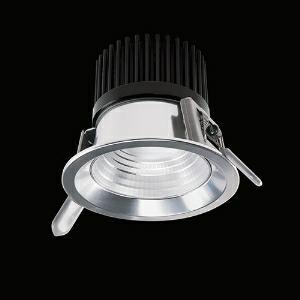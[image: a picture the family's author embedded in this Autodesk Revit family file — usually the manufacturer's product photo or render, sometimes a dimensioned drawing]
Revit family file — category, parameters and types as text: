
# Revit family: spectral_myral_myral_4500-840-f
name_source: partatom
category: Lighting Fixtures
revit_build: Autodesk Revit 2016 (Build: 20150220_1215(x64)
units: mm (PartAtom-declared; Revit-internal decimal feet)

## family parameters
Cut with Voids When Loaded = No
Host = Face
Light Source = No
Part Type = Normal
Room Calculation Point = No
Round Connector Dimension = Use Diameter
Shared = No

## types (1)
- SPECTRAL MYRAL (1 x )
    Apparent Load = 0 VA
    Approval mark = CE
    CIE Flux Codes = 81 99 100 100 100
    Control Gear = Electronic transformer
    Default Elevation = 1800 mm
    Description = SPG0320189
MYRAL recessed spot

Design:
    Height = 0 mm  [stored 0 ft]
    Lamp = 1 x
    Lamp count = 1
    Length = 120 mm
    Luminous efficacy = 0 lm/W
    Manufacturer = Ridi
    ModVariant = No
    Model = MYRAL 4500-840-F
    Mounting Place = Ceiling
    Mounting Type = Recessed
    Number of Poles = 1
    OnlyDefault = Yes
    Power Factor = 1
    Product Name = SPECTRAL MYRAL
    Product group = Downlight recessed
    ProductGroupID = 400
    Protection Class = Protection class
    Protection Degree = IP 20
    RlxData = <blob elided: 38897 chars, md5=2bd27e9b>
    Socket = socket
    Standby Power = 0 W
    System Light Flux = 0 lm
    System Power = 0 W
    Type Image = myral_04.jpg
    URL = http://reluxnet.relux.com
    VarID = ---
    Voltage = 0 V
    Weight = 0.00 kg
    Width = 0 mm  [stored 0 ft]

note: [stored X ft] marks values corroborated as IEEE doubles in the binary element streams (Revit-internal decimal feet)

## geometry (parser evidence)
native form markers: Sweep x10
no freeform markers — native parametric forms only
